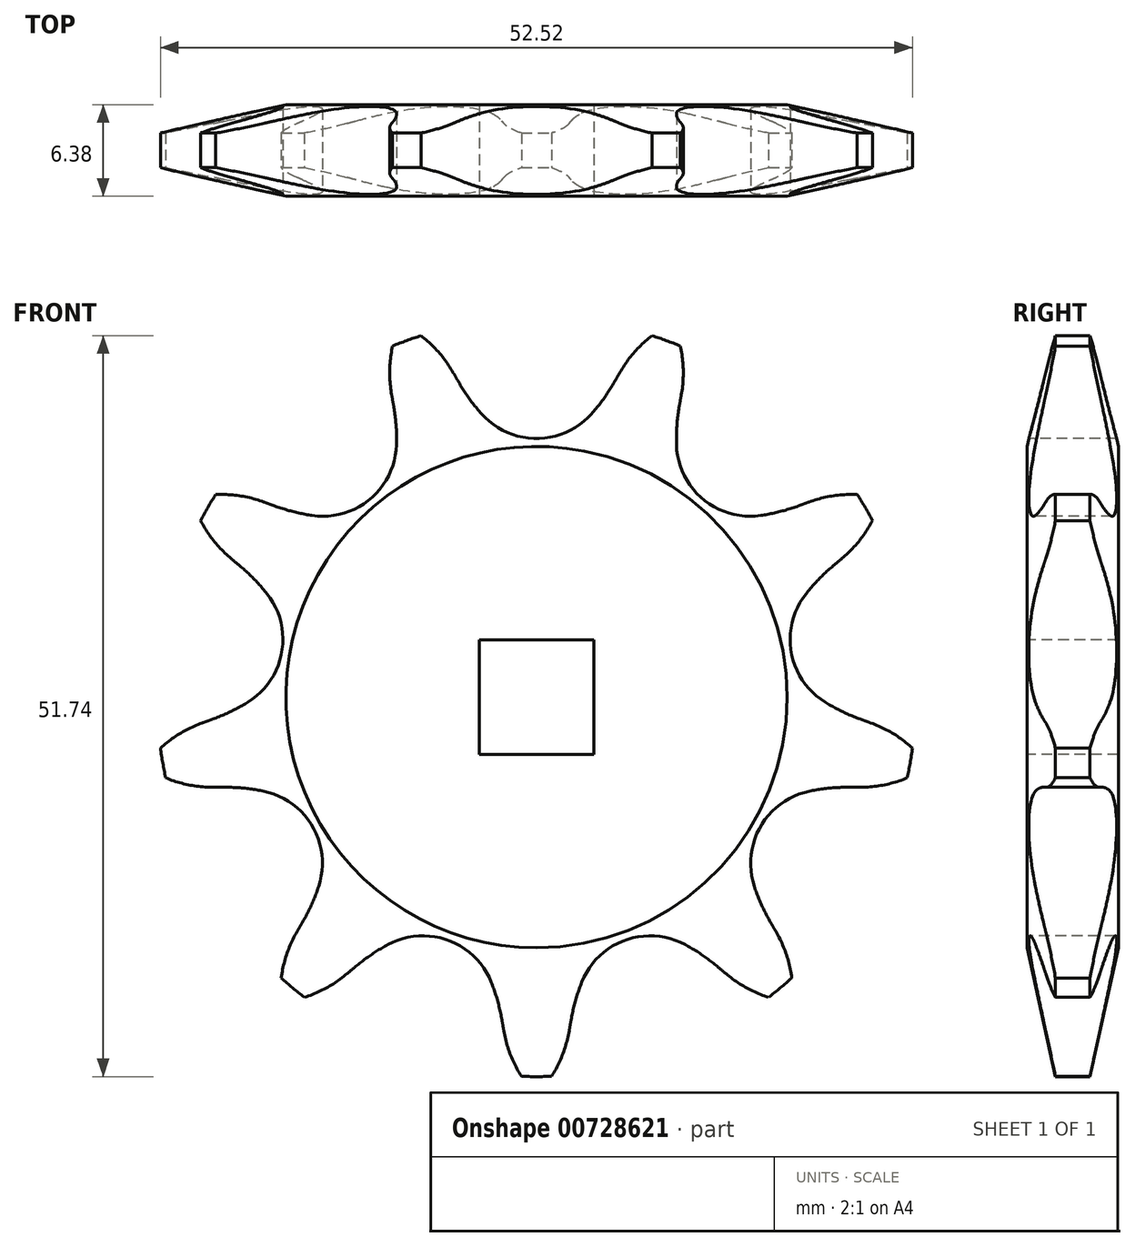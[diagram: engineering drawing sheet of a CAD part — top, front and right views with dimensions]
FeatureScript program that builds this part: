
annotation { "Feature Type Name" : "Feature", "Feature Type Description" : "" }
export const myFeature = defineFeature(function(context is Context, id is Id, definition is map)
    precondition{}
    {
        {
            var Q0;
            Q0=qCreatedBy(makeId("Right.planeOp"),FACE);
            var sketch = newSketch(context, id + "F0", { "sketchPlane" : qUnion([Q0])});
            skLineSegment(sketch, "E0", {"start": v(0, 0) * mm, "end": v(69.6, 0) * mm});
            skLineSegment(sketch, "E1.MirrorCS", {"start": v(0, 0) * mm, "end": v(6.35, 0) * mm});
            skLineSegment(sketch, "E2.MirrorCS", {"start": v(0, -26.5) * mm, "end": v(6.4, -26.5) * mm});
            skLineSegment(sketch, "E3.MirrorCS", {"start": v(0, 0) * mm, "end": v(0, -26.5) * mm});
            skLineSegment(sketch, "E4.MirrorCS", {"start": v(6.35, 0) * mm, "end": v(6.4, -26.5) * mm});
            skSolve(sketch);
        }
        {
            var Q0;
            Q0=makeQuery(id+"F0.imprint","IMPRINT",FACE,{"disambiguationData":[TD([[makeQuery(id+"F0.imprint","IMPRINT",EDGE,{"derivedFrom":sQuery(id+"F0.wireOp",EDGE,"E2.MirrorCS")}),1.0]])]});
            var Q1;
            Q1=sQuery(id+"F0.wireOp",EDGE,"E0");
            revolve(context, id + "F1", {"surfaceOperationType" : NewSurfaceOperationType.NEW, "entities" : qUnion([Q0]), "axis" : qUnion([Q1]), "revolveType" : RevolveType.FULL});
        }
        {
            var Q0;
            Q0=makeQuery(id+"F1.opRevolve","SWEPT_EDGE",EDGE,{"disambiguationData":[OSD([sQuery(id+"F0.wireOp",EDGE,"E2.MirrorCS"),sQuery(id+"F0.wireOp",EDGE,"E4.MirrorCS")])]});
            var Q1;
            Q1=makeQuery(id+"F1.opRevolve","SWEPT_EDGE",EDGE,{"disambiguationData":[OSD([sQuery(id+"F0.wireOp",EDGE,"E2.MirrorCS"),sQuery(id+"F0.wireOp",EDGE,"E3.MirrorCS")])]});
            chamfer(context, id + "F2", {"entities" : qUnion([Q0, Q1]), "chamferType" : ChamferType.TWO_OFFSETS, "width1" : 2 * mm, "oppositeDirection" : false, "width2" : 9 * mm, "tangentPropagation" : true});
        }
        {
            var Q0;
            Q0=makeQuery(id+"F1.opRevolve","SWEPT_FACE",FACE,{"disambiguationData":[OSD([sQuery(id+"F0.wireOp",EDGE,"E3.MirrorCS")])]});
            var sketch = newSketch(context, id + "F3", { "sketchPlane" : qUnion([Q0])});
            skCircle(sketch, "E5", {"center": v(0, 0) * mm, "radius": 23.2 * mm, "construction": true});
            skLineSegment(sketch, "E6", {"start": v(0, 0) * mm, "end": v(0, 23.2) * mm, "construction": true});
            skLineSegment(sketch, "E7", {"start": v(0, 23.2) * mm, "end": v(6.07, 28.61) * mm, "construction": true});
            skLineSegment(sketch, "E8", {"start": v(6.07, 28.61) * mm, "end": v(-5.43, 22) * mm, "construction": true});
            skLineSegment(sketch, "E9", {"start": v(-5.43, 22) * mm, "end": v(-5.43, 22) * mm});
            skLineSegment(sketch, "E10", {"start": v(0, 23.2) * mm, "end": v(19.29, 23.2) * mm, "construction": true});
            skLineSegment(sketch, "E11", {"start": v(0, 0) * mm, "end": v(-9.52, 26.14) * mm, "construction": true});
            skArc(sketch, "E12", {"start": v(-9.52, 26.14) * mm, "mid": v(-19.32, 12) * mm, "end": v(-5.83, 22.68) * mm, "construction": true});
            skArc(sketch, "E13", {"start": v(-5.83, 22.68) * mm, "mid": v(-7.41, 24.68) * mm, "end": v(-9.52, 26.14) * mm});
            skArc(sketch, "E14", {"start": v(-5.43, 22) * mm, "mid": v(-4.7, 20.85) * mm, "end": v(-3.84, 19.79) * mm});
            skArc(sketch, "E15", {"start": v(-3.84, 19.79) * mm, "mid": v(16.84, 36.37) * mm, "end": v(-5.43, 22) * mm, "construction": true});
            skLineSegment(sketch, "E16", {"start": v(-5.43, 22) * mm, "end": v(-5.83, 22.68) * mm});
            skLineSegment(sketch, "E17", {"start": v(-5.83, 22.68) * mm, "end": v(-10, 29.95) * mm, "construction": true});
            skArc(sketch, "E18.MirrorCS", {"start": v(5.83, 22.68) * mm, "mid": v(7.41, 24.68) * mm, "end": v(9.52, 26.14) * mm});
            skLineSegment(sketch, "E19.MirrorCS", {"start": v(5.43, 22) * mm, "end": v(5.83, 22.68) * mm});
            skArc(sketch, "E20.MirrorCS", {"start": v(5.43, 22) * mm, "mid": v(4.7, 20.85) * mm, "end": v(3.84, 19.79) * mm});
            skLineSegment(sketch, "E21", {"start": v(-3.84, 19.79) * mm, "end": v(-3.84, 19.79) * mm});
            skArc(sketch, "E22", {"start": v(3.84, 19.79) * mm, "mid": v(0, 28.35) * mm, "end": v(-3.84, 19.79) * mm, "construction": true});
            skArc(sketch, "E23", {"start": v(-3.84, 19.79) * mm, "mid": v(0, 18.06) * mm, "end": v(3.84, 19.79) * mm});
            skArc(sketch, "E24.1.0", {"start": v(-19.04, 13.63) * mm, "mid": v(-21.55, 14.14) * mm, "end": v(-24.1, 13.91) * mm});
            skArc(sketch, "E24.1.1", {"start": v(-10.11, 21.12) * mm, "mid": v(-10.19, 23.67) * mm, "end": v(-9.52, 26.14) * mm});
            skLineSegment(sketch, "E24.1.2", {"start": v(-9.98, 20.34) * mm, "end": v(-10.11, 21.12) * mm});
            skLineSegment(sketch, "E24.1.3", {"start": v(-18.3, 13.36) * mm, "end": v(-19.04, 13.63) * mm});
            skArc(sketch, "E24.1.4", {"start": v(-18.3, 13.36) * mm, "mid": v(-17, 12.96) * mm, "end": v(-15.66, 12.69) * mm});
            skArc(sketch, "E24.1.5", {"start": v(-15.66, 12.69) * mm, "mid": v(-11.61, 13.84) * mm, "end": v(-9.78, 17.63) * mm});
            skArc(sketch, "E24.1.6", {"start": v(-9.98, 20.34) * mm, "mid": v(-9.8, 19) * mm, "end": v(-9.78, 17.63) * mm});
            skArc(sketch, "E24.2.0", {"start": v(-23.35, -1.8) * mm, "mid": v(-25.6, -3.01) * mm, "end": v(-27.4, -4.83) * mm});
            skArc(sketch, "E24.2.1", {"start": v(-21.32, 9.68) * mm, "mid": v(-23.02, 11.59) * mm, "end": v(-24.1, 13.91) * mm});
            skLineSegment(sketch, "E24.2.2", {"start": v(-20.72, 9.17) * mm, "end": v(-21.32, 9.68) * mm});
            skLineSegment(sketch, "E24.2.3", {"start": v(-22.6, -1.53) * mm, "end": v(-23.35, -1.8) * mm});
            skArc(sketch, "E24.2.4", {"start": v(-22.6, -1.53) * mm, "mid": v(-21.35, -1) * mm, "end": v(-20.16, -0.35) * mm});
            skArc(sketch, "E24.2.5", {"start": v(-20.16, -0.35) * mm, "mid": v(-17.8, 3.14) * mm, "end": v(-18.82, 7.22) * mm});
            skArc(sketch, "E24.2.6", {"start": v(-20.72, 9.17) * mm, "mid": v(-19.72, 8.24) * mm, "end": v(-18.82, 7.22) * mm});
            skArc(sketch, "E24.3.0", {"start": v(-16.73, -16.38) * mm, "mid": v(-17.67, -18.76) * mm, "end": v(-17.88, -21.31) * mm});
            skArc(sketch, "E24.3.1", {"start": v(-22.55, -6.3) * mm, "mid": v(-25.08, -5.92) * mm, "end": v(-27.4, -4.83) * mm});
            skLineSegment(sketch, "E24.3.2", {"start": v(-21.77, -6.3) * mm, "end": v(-22.55, -6.3) * mm});
            skLineSegment(sketch, "E24.3.3", {"start": v(-16.33, -15.7) * mm, "end": v(-16.73, -16.38) * mm});
            skArc(sketch, "E24.3.4", {"start": v(-16.33, -15.7) * mm, "mid": v(-15.71, -14.5) * mm, "end": v(-15.22, -13.22) * mm});
            skArc(sketch, "E24.3.5", {"start": v(-15.22, -13.22) * mm, "mid": v(-15.64, -9.03) * mm, "end": v(-19.06, -6.57) * mm});
            skArc(sketch, "E24.3.6", {"start": v(-21.77, -6.3) * mm, "mid": v(-20.4, -6.36) * mm, "end": v(-19.06, -6.57) * mm});
            skArc(sketch, "E24.4.0", {"start": v(-2.28, -23.3) * mm, "mid": v(-1.48, -25.73) * mm, "end": v(0, -27.82) * mm});
            skArc(sketch, "E24.4.1", {"start": v(-13.23, -19.32) * mm, "mid": v(-15.4, -20.66) * mm, "end": v(-17.88, -21.31) * mm});
            skLineSegment(sketch, "E24.4.2", {"start": v(-12.63, -18.81) * mm, "end": v(-13.23, -19.32) * mm});
            skLineSegment(sketch, "E24.4.3", {"start": v(-2.42, -22.53) * mm, "end": v(-2.28, -23.3) * mm});
            skArc(sketch, "E24.4.4", {"start": v(-2.42, -22.53) * mm, "mid": v(-2.72, -21.2) * mm, "end": v(-3.16, -19.9) * mm});
            skArc(sketch, "E24.4.5", {"start": v(-3.16, -19.9) * mm, "mid": v(-6.18, -16.98) * mm, "end": v(-10.38, -17.28) * mm});
            skArc(sketch, "E24.4.6", {"start": v(-12.63, -18.81) * mm, "mid": v(-11.54, -17.99) * mm, "end": v(-10.38, -17.28) * mm});
            skArc(sketch, "E24.5.0", {"start": v(13.23, -19.32) * mm, "mid": v(15.4, -20.66) * mm, "end": v(17.88, -21.31) * mm});
            skArc(sketch, "E24.5.1", {"start": v(2.28, -23.3) * mm, "mid": v(1.48, -25.73) * mm, "end": v(0, -27.82) * mm});
            skLineSegment(sketch, "E24.5.2", {"start": v(2.42, -22.53) * mm, "end": v(2.28, -23.3) * mm});
            skLineSegment(sketch, "E24.5.3", {"start": v(12.63, -18.81) * mm, "end": v(13.23, -19.32) * mm});
            skArc(sketch, "E24.5.4", {"start": v(12.63, -18.81) * mm, "mid": v(11.54, -17.99) * mm, "end": v(10.38, -17.28) * mm});
            skArc(sketch, "E24.5.5", {"start": v(10.38, -17.28) * mm, "mid": v(6.18, -16.98) * mm, "end": v(3.16, -19.9) * mm});
            skArc(sketch, "E24.5.6", {"start": v(2.42, -22.53) * mm, "mid": v(2.72, -21.2) * mm, "end": v(3.16, -19.9) * mm});
            skArc(sketch, "E24.6.0", {"start": v(22.55, -6.3) * mm, "mid": v(25.08, -5.92) * mm, "end": v(27.4, -4.83) * mm});
            skArc(sketch, "E24.6.1", {"start": v(16.73, -16.38) * mm, "mid": v(17.67, -18.76) * mm, "end": v(17.88, -21.31) * mm});
            skLineSegment(sketch, "E24.6.2", {"start": v(16.33, -15.7) * mm, "end": v(16.73, -16.38) * mm});
            skLineSegment(sketch, "E24.6.3", {"start": v(21.77, -6.3) * mm, "end": v(22.55, -6.3) * mm});
            skArc(sketch, "E24.6.4", {"start": v(21.77, -6.3) * mm, "mid": v(20.4, -6.36) * mm, "end": v(19.06, -6.57) * mm});
            skArc(sketch, "E24.6.5", {"start": v(19.06, -6.57) * mm, "mid": v(15.64, -9.03) * mm, "end": v(15.22, -13.22) * mm});
            skArc(sketch, "E24.6.6", {"start": v(16.33, -15.7) * mm, "mid": v(15.71, -14.5) * mm, "end": v(15.22, -13.22) * mm});
            skArc(sketch, "E24.7.0", {"start": v(21.32, 9.68) * mm, "mid": v(23.02, 11.59) * mm, "end": v(24.1, 13.91) * mm});
            skArc(sketch, "E24.7.1", {"start": v(23.35, -1.8) * mm, "mid": v(25.6, -3.01) * mm, "end": v(27.4, -4.83) * mm});
            skLineSegment(sketch, "E24.7.2", {"start": v(22.6, -1.53) * mm, "end": v(23.35, -1.8) * mm});
            skLineSegment(sketch, "E24.7.3", {"start": v(20.72, 9.17) * mm, "end": v(21.32, 9.68) * mm});
            skArc(sketch, "E24.7.4", {"start": v(20.72, 9.17) * mm, "mid": v(19.72, 8.24) * mm, "end": v(18.82, 7.22) * mm});
            skArc(sketch, "E24.7.5", {"start": v(18.82, 7.22) * mm, "mid": v(17.8, 3.14) * mm, "end": v(20.16, -0.35) * mm});
            skArc(sketch, "E24.7.6", {"start": v(22.6, -1.53) * mm, "mid": v(21.35, -1) * mm, "end": v(20.16, -0.35) * mm});
            skArc(sketch, "E24.8.0", {"start": v(10.11, 21.12) * mm, "mid": v(10.19, 23.67) * mm, "end": v(9.52, 26.14) * mm});
            skArc(sketch, "E24.8.1", {"start": v(19.04, 13.63) * mm, "mid": v(21.55, 14.14) * mm, "end": v(24.1, 13.91) * mm});
            skLineSegment(sketch, "E24.8.2", {"start": v(18.3, 13.36) * mm, "end": v(19.04, 13.63) * mm});
            skLineSegment(sketch, "E24.8.3", {"start": v(9.98, 20.34) * mm, "end": v(10.11, 21.12) * mm});
            skArc(sketch, "E24.8.4", {"start": v(9.98, 20.34) * mm, "mid": v(9.8, 19) * mm, "end": v(9.78, 17.63) * mm});
            skArc(sketch, "E24.8.5", {"start": v(9.78, 17.63) * mm, "mid": v(11.61, 13.84) * mm, "end": v(15.66, 12.69) * mm});
            skArc(sketch, "E24.8.6", {"start": v(18.3, 13.36) * mm, "mid": v(17, 12.96) * mm, "end": v(15.66, 12.69) * mm});
            skCircle(sketch, "E25", {"center": v(22.86, 4.03) * mm, "radius": 7.5 * mm, "construction": true});
            skSolve(sketch);
        }
        {
            var Q0;
            Q0 = qSketchRegion(id + "F3", true);
            extrude(context, id + "F4", {"entities" : qUnion([Q0]), "operationType" : NewBodyOperationType.INTERSECT, "endBound" : BoundingType.THROUGH_ALL, "oppositeDirection" : true, "depth" : 25.4 * mm, "offsetDistance" : 25.4 * mm});
        }
        {
            var Q0;
            {var subQ0=sQuery(id+"F0.wireOp",EDGE,"E3.MirrorCS");Q0=makeQuery(id+"F3.imprint","IMPRINT",FACE,{"disambiguationData":[TD([[makeQuery(id+"F3.imprint","IMPRINT",EDGE,{"derivedFrom":makeQuery(id+"F2.opChamfer","BLEND_EDGE",EDGE,{"blendedFrom":[makeQuery(id+"F1.opRevolve","SWEPT_EDGE",EDGE,{"disambiguationData":[OSD([sQuery(id+"F0.wireOp",EDGE,"E2.MirrorCS"),subQ0])]}),makeQuery(id+"F1.opRevolve","SWEPT_FACE",FACE,{"disambiguationData":[OSD([subQ0])]})],"blendedInto":[makeQuery(id+"F1.opRevolve","SWEPT_FACE",FACE,{"disambiguationData":[OSD([subQ0])]})]})}),1.0]])]});}
            var sketch = newSketch(context, id + "F5", { "sketchPlane" : qUnion([Q0])});
            skLineSegment(sketch, "E26.bottom", {"start": v(-4, -4) * mm, "end": v(4, -4) * mm});
            skLineSegment(sketch, "E26.top", {"start": v(-4, 4) * mm, "end": v(4, 4) * mm});
            skLineSegment(sketch, "E26.left", {"start": v(-4, -4) * mm, "end": v(-4, 4) * mm});
            skLineSegment(sketch, "E26.right", {"start": v(4, -4) * mm, "end": v(4, 4) * mm});
            skPoint(sketch, "E26.middle", {"position": v(0, 0) * mm});
            skSolve(sketch);
        }
        {
            var Q0;
            Q0 = qSketchRegion(id + "F5", true);
            extrude(context, id + "F6", {"entities" : qUnion([Q0]), "operationType" : NewBodyOperationType.REMOVE, "endBound" : BoundingType.THROUGH_ALL, "oppositeDirection" : true, "depth" : 25 * mm, "offsetDistance" : 25 * mm});
        }
    });
